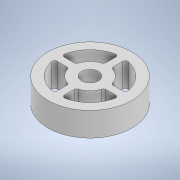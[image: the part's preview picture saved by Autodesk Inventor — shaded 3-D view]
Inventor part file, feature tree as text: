
AUTODESK INVENTOR PART (.ipt)
format: ipt  version: 2020 (Build 240168000, 168)  size: 168,960 bytes
history: native  units: mm
features: extrude x1, fillet x1, sketch x1
ambient origin geometry x8: Origin, YZ Plane, XZ Plane, XY Plane, X Axis, Y Axis, Z Axis, Center Point
bodies: Solid1 (feature_tree)
feature tree (3):
  extrude  "Extrusion1"  Depth=1.0mm
  fillet  "Fillet1"  Radius=4.0mm
  sketch  "Sketch1"  dims[d0=7.0mm d1=35.0mm d2=4.0mm d3=4.0mm d4=3.0mm d5=14.0mm d6=40.0mm d8=360.0deg d10=10.0mm d11=0.0mm d12=1.0mm]
